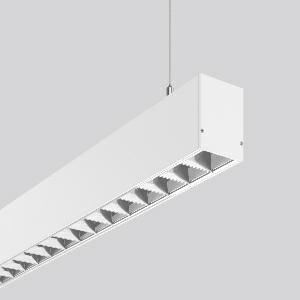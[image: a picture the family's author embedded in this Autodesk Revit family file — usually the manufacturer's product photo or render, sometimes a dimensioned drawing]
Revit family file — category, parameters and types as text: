
# Revit family: less_is_more_50_312336_002_1_76_2639
name_source: partatom
category: Lighting Fixtures
units: mm (PartAtom-declared; Revit-internal decimal feet)

## family parameters
Cut with Voids When Loaded = No
Host = Face
Light Source = No
Part Type = Normal
Room Calculation Point = No
Round Connector Dimension = Use Diameter
Shared = No

## types (1)
- LESS IS MORE 50 (1 x LED Modul 840, 3550 lm, 4000)
    Apparent Load = 28 VA
    CIE Flux Codes = 95 100 100 100 100
    Color Rendering = 80
    Color Temperature = 4000
    Default Elevation = 1800 mm
    Description = Series: LESS IS MORE 50
Linear pendant luminaire for aesthetically sophisticated lighting. Housing: extruded aluminium profile, powder-coated. End cap aluminium powder-coated. Canopy made of aluminium, powder-coated. Alea optical system: Reflector structure (ABS, Aluminium-coated, highly polished) with integrated diffuser made of non-yellowing plastic (PMMA) opal for glare-free light at the workstation (screen-compliant according to EN 12464-1). Direct light emission. Suitable for pendant. 2-point steel cable suspension freely positionable and infinitely height-adjustable. Special lengths available on request. LED unit with integrated converter interchangeable and removable. Suitable for through-wiring. With sensors or as a safety luminaire on request. 
Colour: traffic white, matt (RAL 9016)
Length: 1127 mm
Width: 57 mm
Height: 75 mm
Suspension length: 2000 mm
Lamp: LED
Socket: without socket
Colour temperature: 4000K
Colour rendering index (CRI): 80
System power: 28 W
Rated luminous flux: 3550 lm
Luminous efficiency: 127 lm/W
Control gear: Converter, dimmable, DALI
Protection class: I
Type of protection: IP 20
    Height = 75 mm
    Lamp = 1 x LED Modul 840
    Lamp Light Flux = 3550 lm
    Lamp count = 1
    Length = 1127 mm
    Lifetime = 50000 h
    Luminous efficacy = 127 lm/W
    Manufacturer = RZB
    ModVariant = No
    Model = 312336.002.1.76
    Mounting Place = Ceiling
    Mounting Type = Pendant
    Number of Poles = 1
    OnlyDefault = Yes
    Power Factor = 1
    Product Name = LESS IS MORE 50
    Product group = Pendant LED linear luminaires
    ProductGroupID = 907
    Protection Class = Protection class I
    Protection Degree = IP 20
    RLX_Detail_Level = 1
    RLX_Emergency_Light_Flux = 0 lm
    RLX_Emergency_Type = 0
    RLX_Emergency_Type_DB = No
    RlxData = <blob elided: 33181 chars, md5=701d0a86>
    Socket = socket
    Standby Power = 0 W
    System Light Flux = 3550 lm
    System Power = 28 W
    Type Comments = Product without accessories
    Type Image = 312342.002.jpg
    URL = http://relux.com
    VarID = ---
    Voltage = 230 V
    Voltage Range = 220-240 V
    Weight = 0.00 kg
    Width = 57 mm

## geometry (parser evidence)
native form markers: Blend x4, Sweep x10
no freeform markers — native parametric forms only
